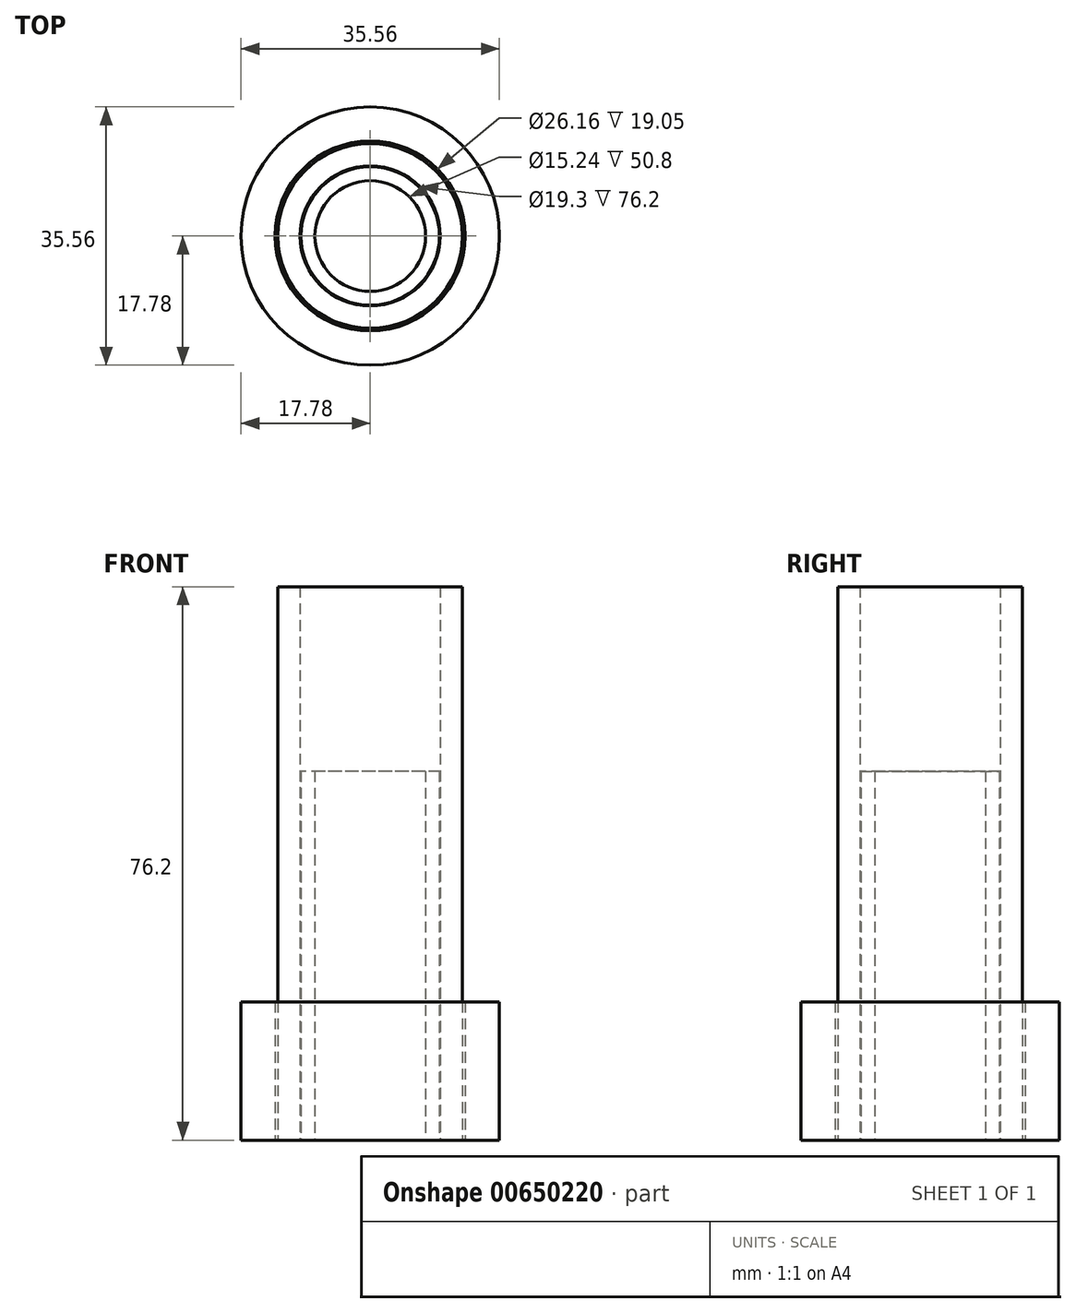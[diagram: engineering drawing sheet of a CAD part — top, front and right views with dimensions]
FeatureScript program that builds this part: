
annotation { "Feature Type Name" : "Feature", "Feature Type Description" : "" }
export const myFeature = defineFeature(function(context is Context, id is Id, definition is map)
    precondition{}
    {
        {
            var Q0;
            Q0=qCreatedBy(makeId("Top.planeOp"),FACE);
            var sketch = newSketch(context, id + "F0", { "sketchPlane" : qUnion([Q0])});
            skCircle(sketch, "E0", {"center": v(0, 0) * mm, "radius": 9.65 * mm});
            skCircle(sketch, "E1", {"center": v(0, 0) * mm, "radius": 12.7 * mm});
            skSolve(sketch);
        }
        {
            var Q0;
            Q0=qCreatedBy(makeId("Top.planeOp"),FACE);
            var sketch = newSketch(context, id + "F1", { "sketchPlane" : qUnion([Q0])});
            skCircle(sketch, "E2", {"center": v(0, 0) * mm, "radius": 9.53 * mm});
            skCircle(sketch, "E3", {"center": v(0, 0) * mm, "radius": 7.62 * mm});
            skSolve(sketch);
        }
        {
            var Q0;
            Q0 = qSketchRegion(id + "F1", true);
            extrude(context, id + "F2", {"entities" : qUnion([Q0]), "depth" : 50.8 * mm, "offsetDistance" : 25.4 * mm});
        }
        {
            var Q0;
            Q0 = qSketchRegion(id + "F0", true);
            extrude(context, id + "F3", {"entities" : qUnion([Q0]), "depth" : 76.2 * mm, "offsetDistance" : 25.4 * mm});
        }
        {
            var Q0;
            Q0=qCreatedBy(makeId("Top.planeOp"),FACE);
            var sketch = newSketch(context, id + "F4", { "sketchPlane" : qUnion([Q0])});
            skCircle(sketch, "E4", {"center": v(0, 0) * mm, "radius": 13.08 * mm});
            skCircle(sketch, "E5", {"center": v(0, 0) * mm, "radius": 17.78 * mm});
            skSolve(sketch);
        }
        {
            var Q0;
            Q0 = qSketchRegion(id + "F4", true);
            extrude(context, id + "F5", {"entities" : qUnion([Q0]), "depth" : 19.05 * mm, "offsetDistance" : 25.4 * mm});
        }
    });
